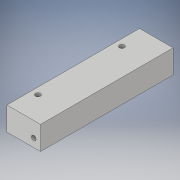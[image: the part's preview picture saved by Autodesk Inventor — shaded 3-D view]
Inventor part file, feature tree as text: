
AUTODESK INVENTOR PART (.ipt)
format: ipt  version: 2019 (Build 230136000, 136)  size: 147,968 bytes
history: native  units: mm
features: extrude x5, sketch x5, other x1, mirror x1, projected_geometry x1
ambient origin geometry x8: Origin, YZ Plane, XZ Plane, XY Plane, X Axis, Y Axis, Z Axis, Center Point
bodies: Body1 (feature_tree)
feature tree (13):
  other  "Твердое тело1"
  extrude  "Выдавливание1"  Depth=20.0mm
  extrude  "Выдавливание2"  Depth=14.0mm
  extrude  "Выдавливание3"  Depth=79.0mm TaperAngle=0.0deg
  mirror  "Зеркальное отражение1"
  extrude  "Выдавливание4"  Depth=2.8mm
  extrude  "Выдавливание5"  Depth=14.0mm TaperAngle=0.0deg
  sketch  "Эскиз1"
  sketch  "Эскиз2"
  sketch  "Эскиз3"
  sketch  "Эскиз4"
  sketch  "Эскиз5"
  projected_geometry  "Спроецированная петля1"
